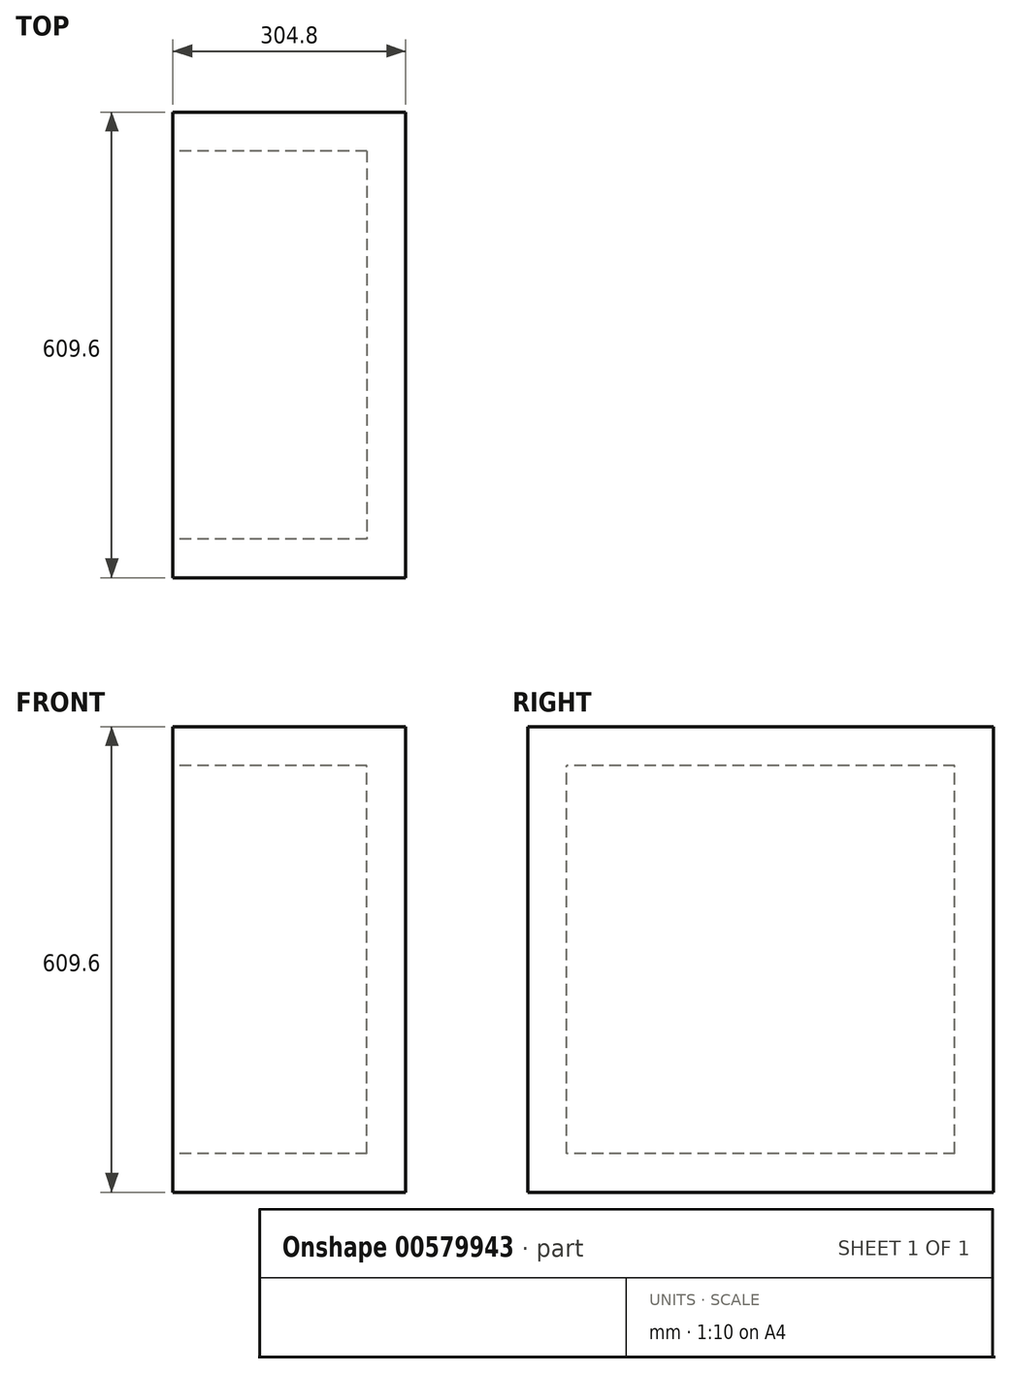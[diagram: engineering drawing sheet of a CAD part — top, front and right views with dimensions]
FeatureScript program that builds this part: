
annotation { "Feature Type Name" : "Feature", "Feature Type Description" : "" }
export const myFeature = defineFeature(function(context is Context, id is Id, definition is map)
    precondition{}
    {
        {
            var Q0;
            Q0=qCreatedBy(makeId("Front.planeOp"),FACE);
            var sketch = newSketch(context, id + "F0", { "sketchPlane" : qUnion([Q0])});
            skLineSegment(sketch, "E0.bottom", {"start": v(-178.78, 193.13) * mm, "end": v(126.02, 193.13) * mm});
            skLineSegment(sketch, "E0.top", {"start": v(-178.78, -416.47) * mm, "end": v(126.02, -416.47) * mm});
            skLineSegment(sketch, "E0.left", {"start": v(-178.78, 193.13) * mm, "end": v(-178.78, -416.47) * mm});
            skLineSegment(sketch, "E0.right", {"start": v(126.02, 193.13) * mm, "end": v(126.02, -416.47) * mm});
            skSolve(sketch);
        }
        {
            var Q0;
            Q0=makeQuery(id+"F0.imprint","IMPRINT",FACE,{"disambiguationData":[TD([[makeQuery(id+"F0.imprint","IMPRINT",EDGE,{"derivedFrom":sQuery(id+"F0.wireOp",EDGE,"E0.bottom")}),-1.0]])]});
            extrude(context, id + "F1", {"entities" : qUnion([Q0]), "depth" : 609.6 * mm, "offsetDistance" : 25.4 * mm});
        }
        {
            var Q0;
            Q0=makeQuery(id+"F1.opExtrude","SWEPT_FACE",FACE,{"disambiguationData":[OSD([sQuery(id+"F0.wireOp",EDGE,"E0.left")])]});
            var sketch = newSketch(context, id + "F2", { "sketchPlane" : qUnion([Q0])});
            skLineSegment(sketch, "E1.bottom", {"start": v(50.8, -365.67) * mm, "end": v(558.8, -365.67) * mm});
            skLineSegment(sketch, "E1.top", {"start": v(50.8, 142.33) * mm, "end": v(558.8, 142.33) * mm});
            skLineSegment(sketch, "E1.left", {"start": v(50.8, -365.67) * mm, "end": v(50.8, 142.33) * mm});
            skLineSegment(sketch, "E1.right", {"start": v(558.8, -365.67) * mm, "end": v(558.8, 142.33) * mm});
            skSolve(sketch);
        }
        {
            var Q0;
            Q0=makeQuery(id+"F2.imprint","IMPRINT",FACE,{"disambiguationData":[TD([[makeQuery(id+"F2.imprint","IMPRINT",EDGE,{"derivedFrom":sQuery(id+"F2.wireOp",EDGE,"E1.bottom")}),1.0]])]});
            extrude(context, id + "F3", {"entities" : qUnion([Q0]), "operationType" : NewBodyOperationType.REMOVE, "oppositeDirection" : true, "depth" : 254 * mm, "offsetDistance" : 25.4 * mm});
        }
    });
